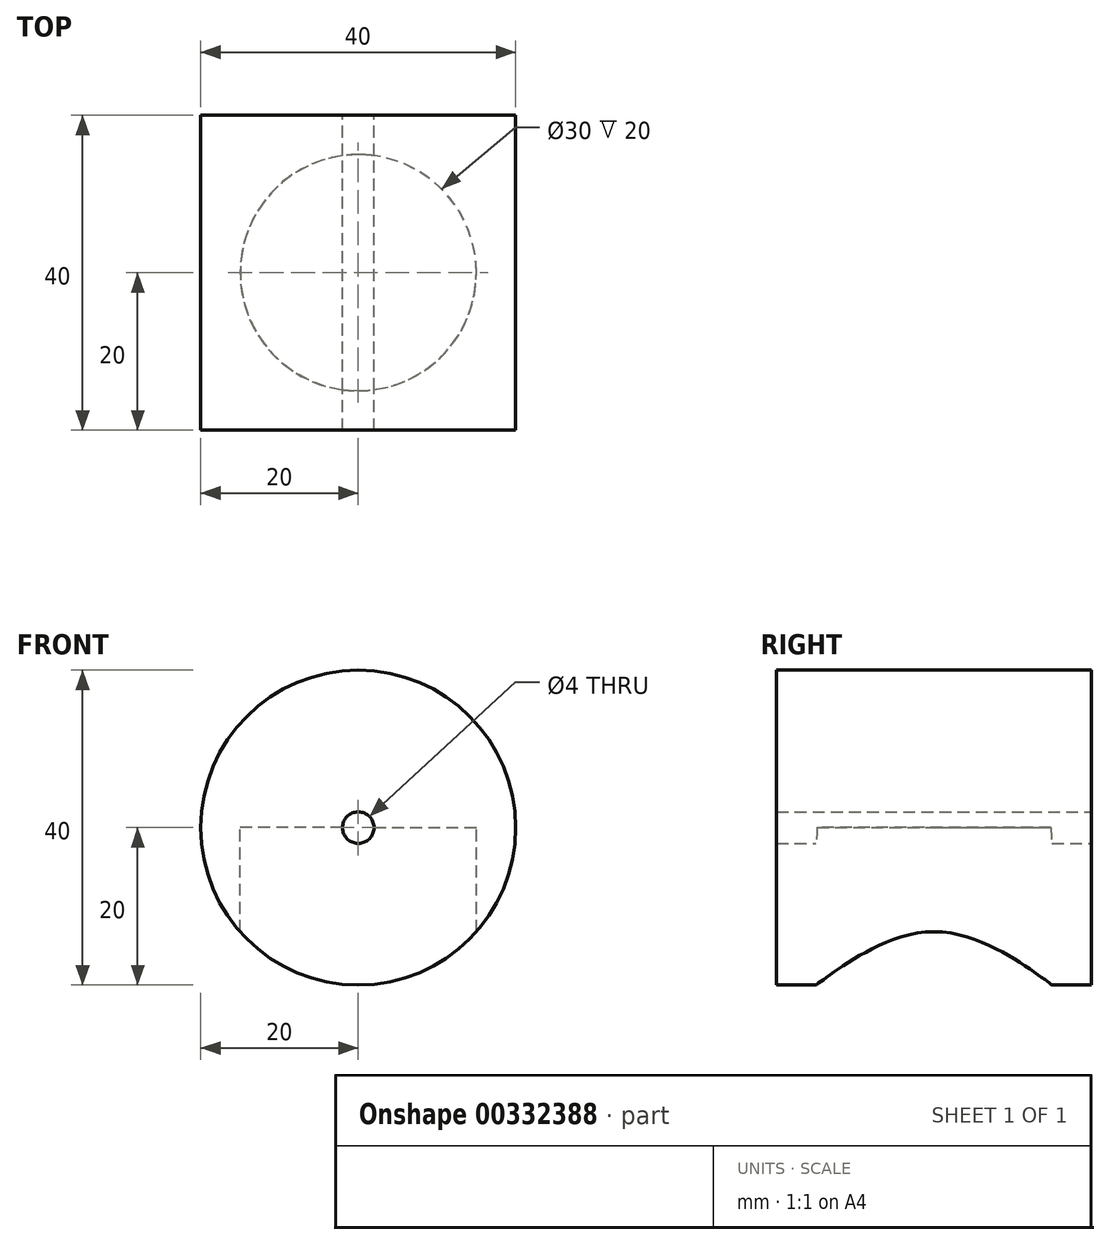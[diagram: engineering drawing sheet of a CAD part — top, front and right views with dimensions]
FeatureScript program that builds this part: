
annotation { "Feature Type Name" : "Feature", "Feature Type Description" : "" }
export const myFeature = defineFeature(function(context is Context, id is Id, definition is map)
    precondition{}
    {
        {
            var Q0;
            Q0=qCreatedBy(makeId("Front.planeOp"),FACE);
            var sketch = newSketch(context, id + "F0", { "sketchPlane" : qUnion([Q0])});
            skCircle(sketch, "E0", {"center": v(0, 0) * mm, "radius": 20 * mm});
            skCircle(sketch, "E1", {"center": v(0, 0) * mm, "radius": 2 * mm});
            skSolve(sketch);
        }
        {
            var Q0;
            Q0=makeQuery(id+"F0.imprint","IMPRINT",FACE,{"disambiguationData":[TD([[makeQuery(id+"F0.imprint","IMPRINT",EDGE,{"derivedFrom":sQuery(id+"F0.wireOp",EDGE,"E0")}),1.0]])]});
            extrude(context, id + "F1", {"entities" : qUnion([Q0]), "depth" : 40 * mm});
        }
        {
            var Q0;
            Q0=qCreatedBy(makeId("Top.planeOp"),FACE);
            var sketch = newSketch(context, id + "F2", { "sketchPlane" : qUnion([Q0])});
            skCircle(sketch, "E2", {"center": v(0, -20) * mm, "radius": 15 * mm});
            skSolve(sketch);
        }
        {
            var Q0;
            Q0 = qSketchRegion(id + "F2", true);
            extrude(context, id + "F3", {"entities" : qUnion([Q0]), "operationType" : NewBodyOperationType.REMOVE, "oppositeDirection" : true, "depth" : 25 * mm});
        }
    });
